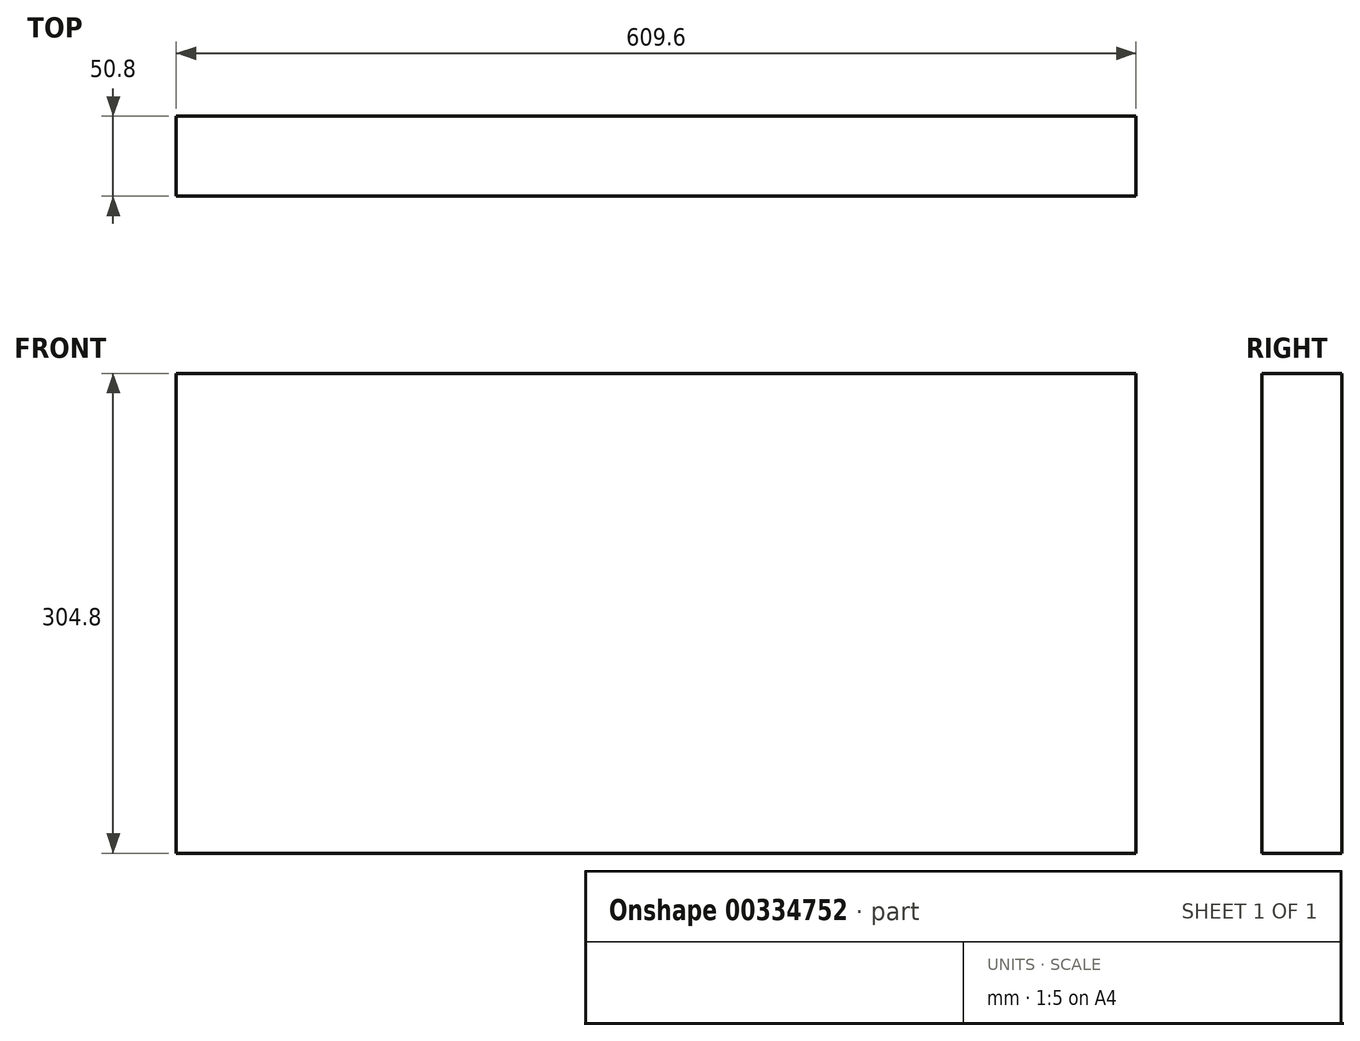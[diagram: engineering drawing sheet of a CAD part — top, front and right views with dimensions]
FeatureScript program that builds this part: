
annotation { "Feature Type Name" : "Feature", "Feature Type Description" : "" }
export const myFeature = defineFeature(function(context is Context, id is Id, definition is map)
    precondition{}
    {
        {
            var Q0;
            Q0=qCreatedBy(makeId("Front.planeOp"),FACE);
            var sketch = newSketch(context, id + "F0", { "sketchPlane" : qUnion([Q0])});
            skLineSegment(sketch, "E0.bottom", {"start": v(-305.92, 46.88) * mm, "end": v(303.68, 46.88) * mm});
            skLineSegment(sketch, "E0.top", {"start": v(-305.92, -257.92) * mm, "end": v(303.68, -257.92) * mm});
            skLineSegment(sketch, "E0.left", {"start": v(-305.92, 46.88) * mm, "end": v(-305.92, -257.92) * mm});
            skLineSegment(sketch, "E0.right", {"start": v(303.68, 46.88) * mm, "end": v(303.68, -257.92) * mm});
            skSolve(sketch);
        }
        {
            var Q0;
            Q0 = qSketchRegion(id + "F0", true);
            extrude(context, id + "F1", {"entities" : qUnion([Q0]), "depth" : 50.8 * mm});
        }
    });
